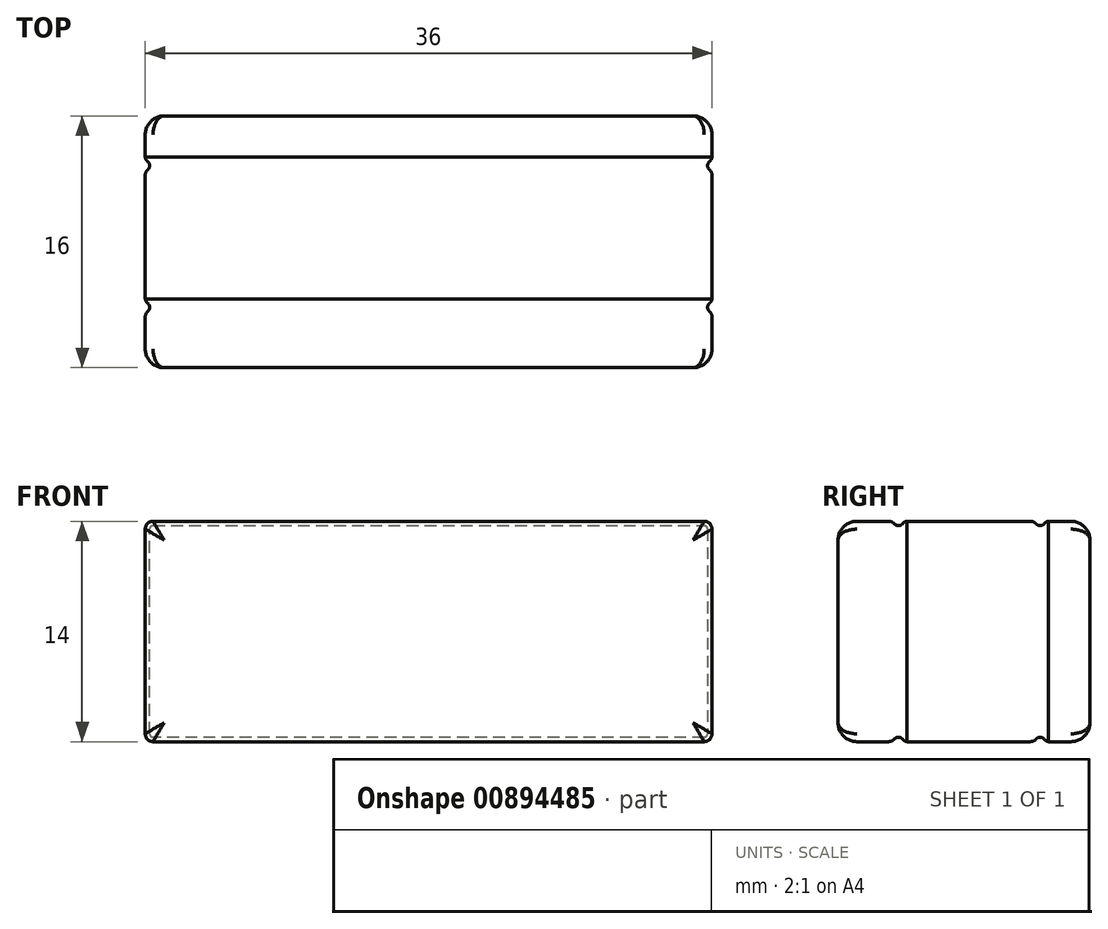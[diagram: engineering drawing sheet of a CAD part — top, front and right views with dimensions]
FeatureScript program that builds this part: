
annotation { "Feature Type Name" : "Feature", "Feature Type Description" : "" }
export const myFeature = defineFeature(function(context is Context, id is Id, definition is map)
    precondition{}
    {
        {
            var Q0;
            Q0=qCreatedBy(makeId("Top.planeOp"),FACE);
            var sketch = newSketch(context, id + "F0", { "sketchPlane" : qUnion([Q0])});
            skLineSegment(sketch, "E0.bottom", {"start": v(-18, 8) * mm, "end": v(18, 8) * mm});
            skLineSegment(sketch, "E0.top", {"start": v(-18, -8) * mm, "end": v(18, -8) * mm});
            skLineSegment(sketch, "E0.left", {"start": v(-18, 8) * mm, "end": v(-18, -8) * mm});
            skLineSegment(sketch, "E0.right", {"start": v(18, 8) * mm, "end": v(18, -8) * mm});
            skSolve(sketch);
        }
        {
            var Q0;
            Q0=makeQuery(id+"F0.imprint","IMPRINT",FACE,{"disambiguationData":[TD([[makeQuery(id+"F0.imprint","IMPRINT",EDGE,{"derivedFrom":sQuery(id+"F0.wireOp",EDGE,"E0.bottom")}),-1.0]])]});
            extrude(context, id + "F1", {"entities" : qUnion([Q0]), "depth" : 14 * mm, "offsetDistance" : 25 * mm});
        }
        {
            var Q0;
            Q0=makeQuery(id+"F1.opExtrude","CAP_EDGE",EDGE,{"disambiguationData":[OSD([sQuery(id+"F0.wireOp",EDGE,"E0.top")])],"isStart":false});
            var Q1;
            Q1=makeQuery(id+"F1.opExtrude","CAP_EDGE",EDGE,{"disambiguationData":[OSD([sQuery(id+"F0.wireOp",EDGE,"E0.bottom")])],"isStart":false});
            var Q2;
            Q2=makeQuery(id+"F1.opExtrude","SWEPT_EDGE",EDGE,{"disambiguationData":[OSD([sQuery(id+"F0.wireOp",EDGE,"E0.top"),sQuery(id+"F0.wireOp",EDGE,"E0.left")])]});
            var Q3;
            Q3=makeQuery(id+"F1.opExtrude","SWEPT_EDGE",EDGE,{"disambiguationData":[OSD([sQuery(id+"F0.wireOp",EDGE,"E0.top"),sQuery(id+"F0.wireOp",EDGE,"E0.right")])]});
            var Q4;
            Q4=makeQuery(id+"F1.opExtrude","SWEPT_EDGE",EDGE,{"disambiguationData":[OSD([sQuery(id+"F0.wireOp",EDGE,"E0.bottom"),sQuery(id+"F0.wireOp",EDGE,"E0.right")])]});
            var Q5;
            Q5=makeQuery(id+"F1.opExtrude","CAP_EDGE",EDGE,{"disambiguationData":[OSD([sQuery(id+"F0.wireOp",EDGE,"E0.top")])],"isStart":true});
            var Q6;
            Q6=makeQuery(id+"F1.opExtrude","SWEPT_EDGE",EDGE,{"disambiguationData":[OSD([sQuery(id+"F0.wireOp",EDGE,"E0.bottom"),sQuery(id+"F0.wireOp",EDGE,"E0.left")])]});
            var Q7;
            Q7=makeQuery(id+"F1.opExtrude","CAP_EDGE",EDGE,{"disambiguationData":[OSD([sQuery(id+"F0.wireOp",EDGE,"E0.bottom")])],"isStart":true});
            fillet(context, id + "F2", {"entities" : qUnion([Q0, Q1, Q2, Q3, Q4, Q5, Q6, Q7]), "radius" : 1.2 * mm, "tangentPropagation" : true, "allowEdgeOverflow" : false});
        }
        {
            var Q0;
            Q0=makeQuery(id+"F1.opExtrude","CAP_EDGE",EDGE,{"disambiguationData":[OSD([sQuery(id+"F0.wireOp",EDGE,"E0.right")])],"isStart":true});
            var Q1;
            Q1=makeQuery(id+"F1.opExtrude","CAP_EDGE",EDGE,{"disambiguationData":[OSD([sQuery(id+"F0.wireOp",EDGE,"E0.right")])],"isStart":false});
            var Q2;
            Q2=makeQuery(id+"F1.opExtrude","CAP_EDGE",EDGE,{"disambiguationData":[OSD([sQuery(id+"F0.wireOp",EDGE,"E0.left")])],"isStart":false});
            var Q3;
            Q3=makeQuery(id+"F1.opExtrude","CAP_EDGE",EDGE,{"disambiguationData":[OSD([sQuery(id+"F0.wireOp",EDGE,"E0.left")])],"isStart":true});
            fillet(context, id + "F3", {"entities" : qUnion([Q0, Q1, Q2, Q3]), "radius" : 0.5 * mm, "tangentPropagation" : true, "allowEdgeOverflow" : false});
        }
        {
            var Q0;
            Q0=qCreatedBy(makeId("Front.planeOp"),FACE);
            cPlane(context, id + "F4", {"entities" : qUnion([Q0]), "cplaneType" : CPlaneType.OFFSET, "offset" : 4 * mm, "width" : 150 * mm, "height" : 150 * mm});
        }
        {
            var Q0;
            Q0=qCreatedBy(id+"F4.planeOp",FACE);
            var sketch = newSketch(context, id + "F5", { "sketchPlane" : qUnion([Q0])});
            skLineSegment(sketch, "E1.0", {"start": v(-17.5, 14) * mm, "end": v(17.5, 14) * mm});
            skPoint(sketch, "E2.0", {"position": v(-17.85, 13.85) * mm});
            skArc(sketch, "E3.0", {"start": v(-17.5, 14) * mm, "mid": v(-17.85, 13.85) * mm, "end": v(-18, 13.5) * mm});
            skLineSegment(sketch, "E4.0", {"start": v(-18, 0.5) * mm, "end": v(-18, 13.5) * mm});
            skArc(sketch, "E5.0", {"start": v(-18, 0.5) * mm, "mid": v(-17.85, 0.15) * mm, "end": v(-17.5, 0) * mm});
            skLineSegment(sketch, "E6.0", {"start": v(17.5, 0) * mm, "end": v(-17.5, 0) * mm});
            skArc(sketch, "E7.0", {"start": v(17.5, 0) * mm, "mid": v(17.85, 0.15) * mm, "end": v(18, 0.5) * mm});
            skLineSegment(sketch, "E8.0", {"start": v(18, 13.5) * mm, "end": v(18, 0.5) * mm});
            skArc(sketch, "E9.0", {"start": v(18, 13.5) * mm, "mid": v(17.85, 13.85) * mm, "end": v(17.5, 14) * mm});
            skSolve(sketch);
        }
        {
            var Q0;
            Q0=qCreatedBy(makeId("Right.planeOp"),FACE);
            var sketch = newSketch(context, id + "F6", { "sketchPlane" : qUnion([Q0])});
            skArc(sketch, "E10", {"start": v(-4.42, 13.83) * mm, "mid": v(-4.16, 13.72) * mm, "end": v(-3.9, 13.84) * mm});
            skArc(sketch, "E11", {"start": v(-3.54, 14) * mm, "mid": v(-3.74, 13.96) * mm, "end": v(-3.9, 13.84) * mm});
            skArc(sketch, "E12", {"start": v(-4.42, 13.83) * mm, "mid": v(-4.58, 13.96) * mm, "end": v(-4.78, 14) * mm});
            skLineSegment(sketch, "E13", {"start": v(-3.54, 14) * mm, "end": v(-4.78, 14) * mm});
            skLineSegment(sketch, "E14.1.0.0", {"start": v(5.46, 14) * mm, "end": v(4.22, 14) * mm});
            skArc(sketch, "E14.1.0.1", {"start": v(4.58, 13.83) * mm, "mid": v(4.42, 13.96) * mm, "end": v(4.22, 14) * mm});
            skArc(sketch, "E14.1.0.2", {"start": v(5.46, 14) * mm, "mid": v(5.26, 13.96) * mm, "end": v(5.1, 13.84) * mm});
            skLineSegment(sketch, "E14.direction1", {"start": v(-4.78, 13.52) * mm, "end": v(4.22, 13.52) * mm, "construction": true});
            skArc(sketch, "E15", {"start": v(4.58, 13.83) * mm, "mid": v(4.84, 13.72) * mm, "end": v(5.1, 13.84) * mm});
            skSolve(sketch);
        }
        {
            var Q0;
            Q0 = qSketchRegion(id + "F6", true);
            var Q1;
            Q1 = qConstructionFilter(qBodyType(qCreatedBy(id + "F5" ,EDGE), BodyType.WIRE), ConstructionObject.NO);
            sweep(context, id + "F7", {"operationType" : NewBodyOperationType.REMOVE, "profiles" : qUnion([Q0]), "path" : qUnion([Q1])});
        }
    });
